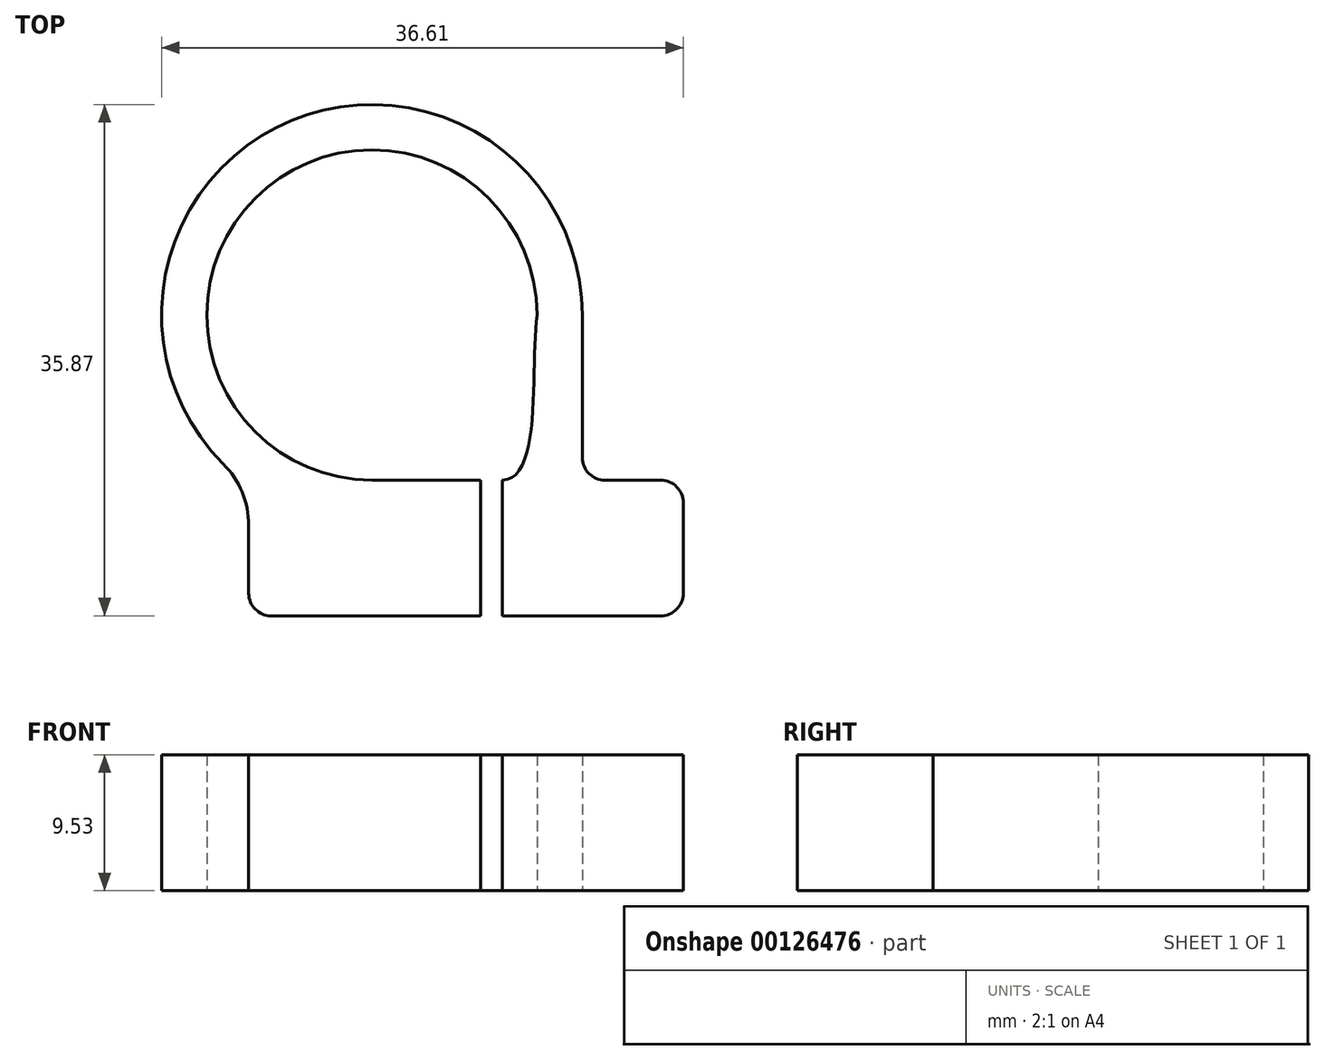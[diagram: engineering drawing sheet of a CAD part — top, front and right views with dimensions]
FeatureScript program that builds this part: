
annotation { "Feature Type Name" : "Feature", "Feature Type Description" : "" }
export const myFeature = defineFeature(function(context is Context, id is Id, definition is map)
    precondition{}
    {
        {
            var Q0;
            Q0=qCreatedBy(makeId("Top.planeOp"),FACE);
            var sketch = newSketch(context, id + "F0", { "sketchPlane" : qUnion([Q0])});
            skCircle(sketch, "E0", {"center": v(0, 0) * mm, "radius": 10.8 * mm, "construction": true});
            skCircle(sketch, "E1", {"center": v(0, 0) * mm, "radius": 11.59 * mm, "construction": true});
            skPoint(sketch, "E2", {"position": v(0, -10.8) * mm});
            skCircle(sketch, "E3", {"center": v(0, 0) * mm, "radius": 14.76 * mm, "construction": true});
            skPoint(sketch, "E4", {"position": v(0, 14.76) * mm});
            skLineSegment(sketch, "E5", {"start": v(0, 0) * mm, "end": v(0, 14.76) * mm, "construction": true});
            skLineSegment(sketch, "E6", {"start": v(-14.76, 0) * mm, "end": v(14.76, 0) * mm, "construction": true});
            skLineSegment(sketch, "E7", {"start": v(0, 0) * mm, "end": v(0, -10.8) * mm, "construction": true});
            skLineSegment(sketch, "E8", {"start": v(0, 0) * mm, "end": v(-10.44, -10.44) * mm, "construction": true});
            skLineSegment(sketch, "E9", {"start": v(0, -11.59) * mm, "end": v(21.85, -11.59) * mm, "construction": true});
            skLineSegment(sketch, "E10", {"start": v(0, -11.59) * mm, "end": v(-31.95, -11.59) * mm, "construction": true});
            skPoint(sketch, "E11", {"position": v(10.8, 0) * mm});
            skPoint(sketch, "E12", {"position": v(11.59, 0) * mm});
            skPoint(sketch, "E13", {"position": v(14.76, 0) * mm});
            skPoint(sketch, "E14", {"position": v(-8.2, -8.2) * mm});
            skArc(sketch, "E15", {"start": v(11.59, 0) * mm, "mid": v(-8.2, 8.2) * mm, "end": v(0, -11.59) * mm});
            skArc(sketch, "E16", {"start": v(14.76, 0) * mm, "mid": v(-5.65, 13.64) * mm, "end": v(-10.44, -10.44) * mm});
            skArc(sketch, "E17", {"start": v(-8.65, -14.76) * mm, "mid": v(-9.11, -12.42) * mm, "end": v(-10.44, -10.44) * mm});
            skLineSegment(sketch, "E18", {"start": v(0, -14.76) * mm, "end": v(-29.4, -14.76) * mm, "construction": true});
            skLineSegment(sketch, "E19", {"start": v(0, -11.59) * mm, "end": v(7.62, -11.59) * mm});
            skLineSegment(sketch, "E20", {"start": v(7.62, -11.59) * mm, "end": v(7.62, -21.11) * mm});
            skLineSegment(sketch, "E21", {"start": v(7.62, -21.11) * mm, "end": v(-7.06, -21.11) * mm});
            skLineSegment(sketch, "E22", {"start": v(-8.65, -14.76) * mm, "end": v(-8.65, -19.53) * mm});
            skLineSegment(sketch, "E23.bottom", {"start": v(7.62, -21.11) * mm, "end": v(9.15, -21.11) * mm, "construction": true});
            skLineSegment(sketch, "E23.top", {"start": v(7.62, -11.59) * mm, "end": v(9.15, -11.59) * mm, "construction": true});
            skLineSegment(sketch, "E23.left", {"start": v(7.62, -21.11) * mm, "end": v(7.62, -11.59) * mm});
            skFitSpline(sketch, "E24", {"points": [v(9.15, -11.59) * mm, v(11.59, 0) * mm], "startDerivative": vector(8.62, 0) * mm, "endDerivative": vector(1.47, 10) * mm});
            skLineSegment(sketch, "E25.bottom", {"start": v(9.15, -21.11) * mm, "end": v(20.26, -21.11) * mm});
            skLineSegment(sketch, "E25.left", {"start": v(9.15, -21.11) * mm, "end": v(9.15, -11.59) * mm});
            skLineSegment(sketch, "E25.right", {"start": v(21.85, -19.53) * mm, "end": v(21.85, -13.18) * mm});
            skLineSegment(sketch, "E26", {"start": v(14.76, 0) * mm, "end": v(14.76, -10) * mm});
            skLineSegment(sketch, "E27.trimOffspring", {"start": v(16.35, -11.59) * mm, "end": v(20.26, -11.59) * mm});
            skPoint(sketch, "E28.visualSharp", {"position": v(-8.65, -21.11) * mm});
            skArc(sketch, "E28.filletArc", {"start": v(-8.65, -19.53) * mm, "mid": v(-8.18, -20.65) * mm, "end": v(-7.06, -21.11) * mm});
            skPoint(sketch, "E29.visualSharp", {"position": v(21.85, -21.11) * mm});
            skArc(sketch, "E29.filletArc", {"start": v(20.26, -21.11) * mm, "mid": v(21.38, -20.65) * mm, "end": v(21.85, -19.53) * mm});
            skPoint(sketch, "E30.visualSharp", {"position": v(21.85, -11.59) * mm});
            skArc(sketch, "E31.filletArc", {"start": v(21.85, -13.18) * mm, "mid": v(21.38, -12.05) * mm, "end": v(20.26, -11.59) * mm});
            skPoint(sketch, "E32.visualSharp", {"position": v(14.76, -11.59) * mm});
            skArc(sketch, "E32.filletArc", {"start": v(14.76, -10) * mm, "mid": v(15.23, -11.12) * mm, "end": v(16.35, -11.59) * mm});
            skLineSegment(sketch, "E33", {"start": v(0, -10.8) * mm, "end": v(0, -14.76) * mm, "construction": true});
            skLineSegment(sketch, "E34", {"start": v(14.76, 0) * mm, "end": v(14.76, -11.59) * mm, "construction": true});
            skLineSegment(sketch, "E35", {"start": v(21.85, -19.53) * mm, "end": v(21.85, -11.59) * mm, "construction": true});
            skSolve(sketch);
        }
        {
            var Q0;
            Q0=makeQuery(id+"F0.imprint","IMPRINT",FACE,{"disambiguationData":[TD([[makeQuery(id+"F0.imprint","IMPRINT",EDGE,{"derivedFrom":sQuery(id+"F0.wireOp",EDGE,"E15")}),-1.0]])]});
            extrude(context, id + "F1", {"entities" : qUnion([Q0]), "depth" : 9.52 * mm});
        }
    });
